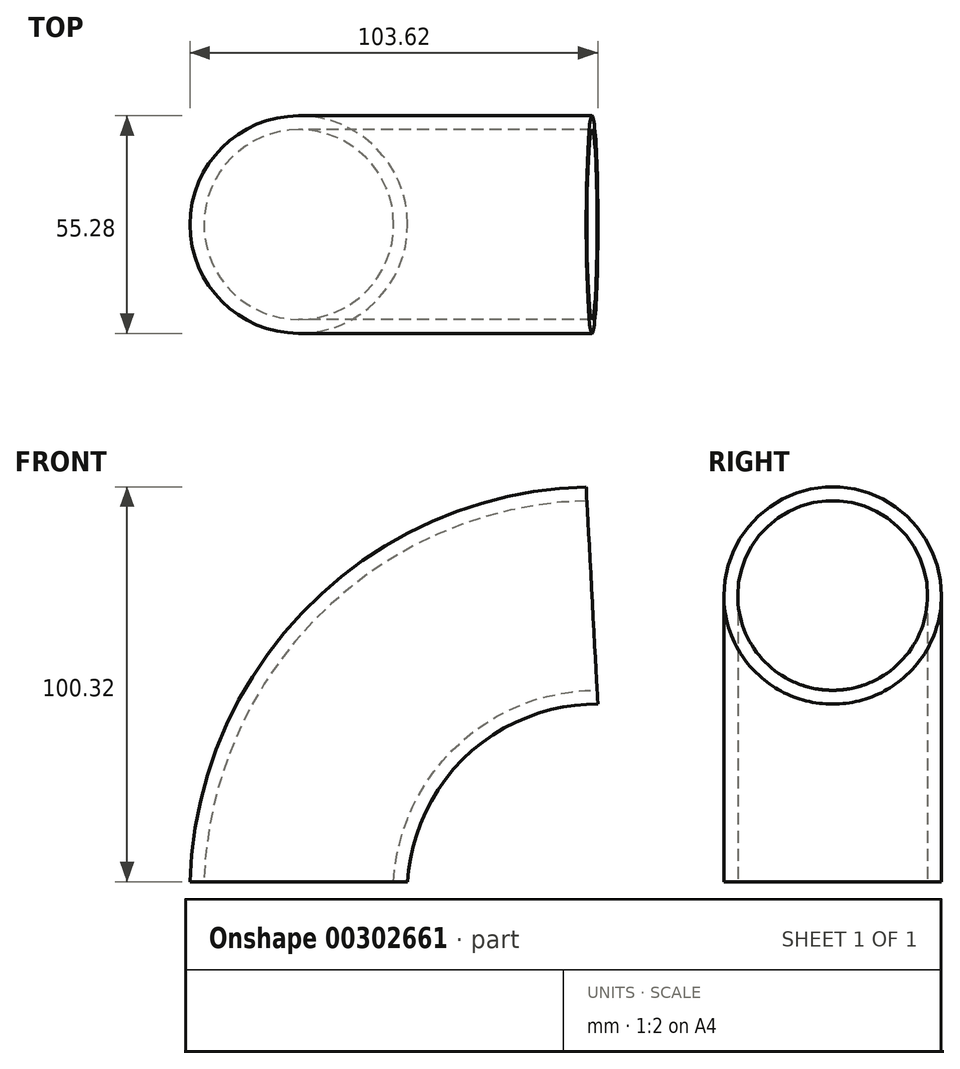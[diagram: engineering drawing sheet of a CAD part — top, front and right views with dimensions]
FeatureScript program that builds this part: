
annotation { "Feature Type Name" : "Feature", "Feature Type Description" : "" }
export const myFeature = defineFeature(function(context is Context, id is Id, definition is map)
    precondition{}
    {
        {
            var Q0;
            Q0=qCreatedBy(makeId("Top.planeOp"),FACE);
            var sketch = newSketch(context, id + "F0", { "sketchPlane" : qUnion([Q0])});
            skCircle(sketch, "E0", {"center": v(0, 0) * mm, "radius": 27.64 * mm});
            skCircle(sketch, "E1", {"center": v(0, 0) * mm, "radius": 24.11 * mm});
            skSolve(sketch);
        }
        {
            var Q0;
            Q0=qCreatedBy(makeId("Front.planeOp"),FACE);
            var sketch = newSketch(context, id + "F1", { "sketchPlane" : qUnion([Q0])});
            skArc(sketch, "E2", {"start": v(74.5, 72.72) * mm, "mid": v(22.76, 51.2) * mm, "end": v(0, 0) * mm});
            skSolve(sketch);
        }
        {
            var Q0;
            Q0=makeQuery(id+"F0.imprint","IMPRINT",FACE,{"disambiguationData":[TD([[makeQuery(id+"F0.imprint","IMPRINT",EDGE,{"derivedFrom":sQuery(id+"F0.wireOp",EDGE,"E0")}),1.0]])]});
            var Q1;
            Q1=sQuery(id+"F1.wireOp",EDGE,"E2");
            sweep(context, id + "F2", {"profiles" : qUnion([Q0]), "path" : qUnion([Q1])});
        }
    });
